# Revit family: Klik
name_source: partatom
category: Furniture
revit_build: Autodesk Revit 2015 (Build: 20140606_1530(x64)
units: mm (PartAtom-declared; Revit-internal decimal feet)

## types (12) — shared parameters
Manufacturer = Isku Oy
Table height = 730 mm  [stored 2.39501 ft]
Table thickness = 26 mm
URL = www.isku.fi

## per-type parameters (varying)
| type | Leg distance in x direction | Length | Table legs | Table top  type | Width |
| Klik 2531 - Table top A12 | 1100 mm | 1200 mm | klik 2531 leg : 2531 For A tops | Table top A : A12 | 800 mm  [stored 2.62467 ft] |
| Klik 2531 - Table top A14 | 1300 mm  [stored 4.26509 ft] | 1400 mm  [stored 4.59318 ft] | klik 2531 leg : 2531 For A tops | Table top A : A14 | 800 mm  [stored 2.62467 ft] |
| Klik 2531 - Table top A16 | 1500 mm  [stored 4.92126 ft] | 1600 mm  [stored 5.24934 ft] | klik 2531 leg : 2531 For A tops | Table top A : A16 | 800 mm  [stored 2.62467 ft] |
| Klik 2531 - Table top A10 | 900 mm  [stored 2.95276 ft] | 1000 mm  [stored 3.28084 ft] | klik 2531 leg : 2531 For A tops | Table top A : A10 | 800 mm  [stored 2.62467 ft] |
| Klik 2531 - Table top B10 | 900 mm  [stored 2.95276 ft] | 1000 mm  [stored 3.28084 ft] | klik 2531 leg : 2531 For B tops | Table top B : B10 | 600 mm  [stored 1.9685 ft] |
| Klik 2531 - Table top B12 | 1100 mm | 1200 mm | klik 2531 leg : 2531 For B tops | Table top B : B12 | 600 mm  [stored 1.9685 ft] |
| Klik 2531 - Table top B14 | 1300 mm  [stored 4.26509 ft] | 1400 mm  [stored 4.59318 ft] | klik 2531 leg : 2531 For B tops | Table top B : B14 | 600 mm  [stored 1.9685 ft] |
| Klik 2531 - Table top B16 | 1500 mm  [stored 4.92126 ft] | 1600 mm  [stored 5.24934 ft] | klik 2531 leg : 2531 For B tops | Table top B : B16 | 600 mm  [stored 1.9685 ft] |
| Klik 2531 - Table top C10 | 900 mm  [stored 2.95276 ft] | 1000 mm  [stored 3.28084 ft] | klik 2531 leg : 2531 For C tops | Table top C : C10 | 600 mm  [stored 1.9685 ft] |
| Klik 2531 - Table top C12 | 1100 mm | 1200 mm | klik 2531 leg : 2531 For C tops | Table top C : C12 | 600 mm  [stored 1.9685 ft] |
| Klik 2531 - Table top C14 | 1300 mm  [stored 4.26509 ft] | 1400 mm  [stored 4.59318 ft] | klik 2531 leg : 2531 For C tops | Table top C : C14 | 600 mm  [stored 1.9685 ft] |
| Klik 2531 - Table top C16 | 1500 mm  [stored 4.92126 ft] | 1600 mm  [stored 5.24934 ft] | klik 2531 leg : 2531 For C tops | Table top C : C16 | 600 mm  [stored 1.9685 ft] |

note: [stored X ft] marks values corroborated as IEEE doubles in the binary element streams (Revit-internal decimal feet)

## geometry (parser evidence)
native form markers: Sweep x18
no freeform markers — native parametric forms only
